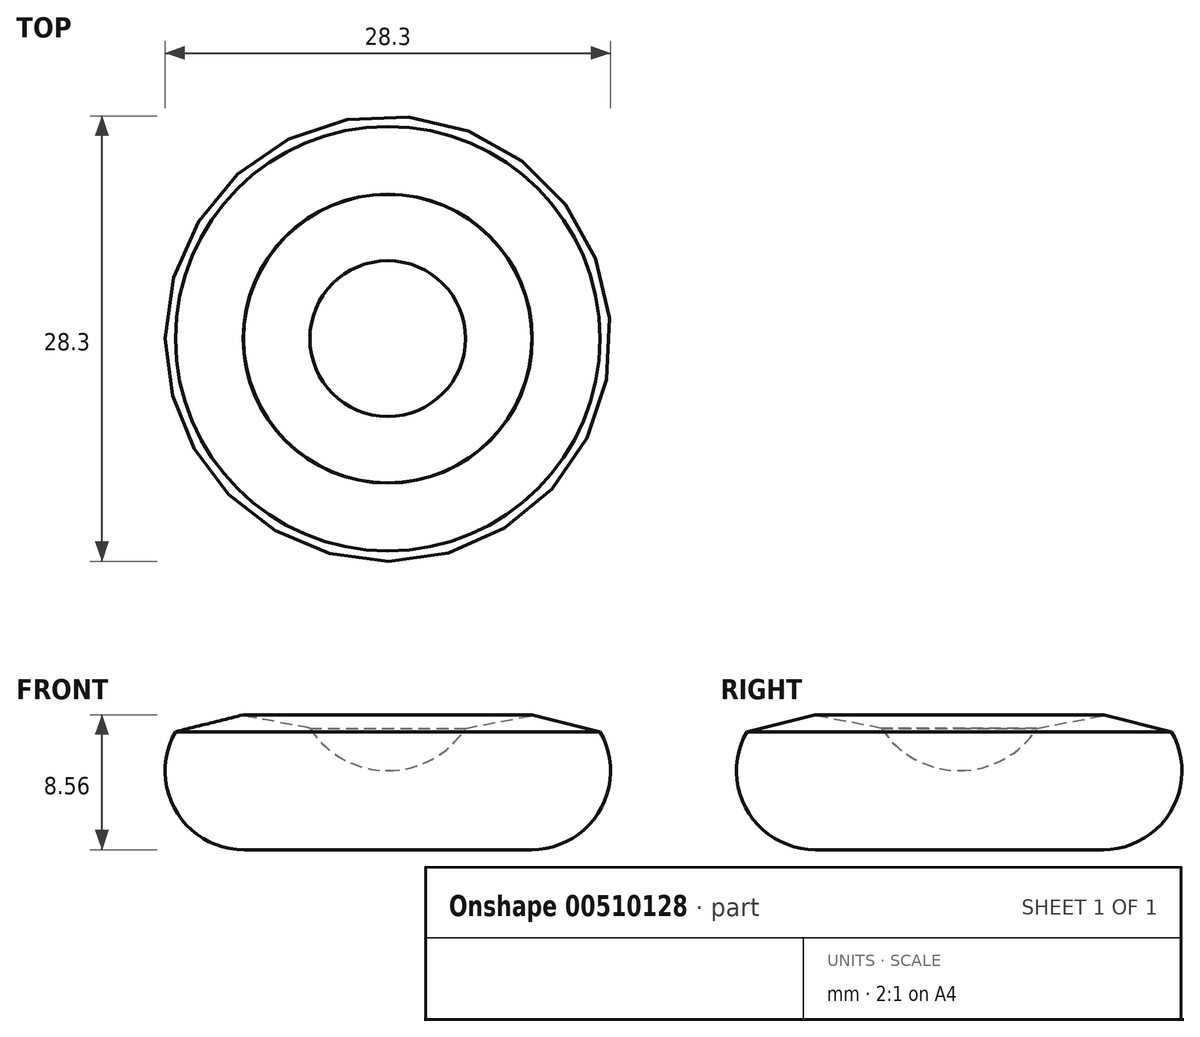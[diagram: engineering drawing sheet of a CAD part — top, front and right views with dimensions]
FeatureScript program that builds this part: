
annotation { "Feature Type Name" : "Feature", "Feature Type Description" : "" }
export const myFeature = defineFeature(function(context is Context, id is Id, definition is map)
    precondition{}
    {
        {
            var Q0;
            Q0=qCreatedBy(makeId("Front.planeOp"),FACE);
            var sketch = newSketch(context, id + "F0", { "sketchPlane" : qUnion([Q0])});
            skPoint(sketch, "E0.center.orphan", {"position": v(-21.03, 0) * mm});
            skPoint(sketch, "E1.center.orphan", {"position": v(-13.36, 0) * mm});
            skPoint(sketch, "E2.center.orphan", {"position": v(0, 5) * mm});
            skPoint(sketch, "E3.start.orphan", {"position": v(0, 1.96) * mm});
            skPoint(sketch, "E4.start.orphan", {"position": v(0, -5.22) * mm});
            skArc(sketch, "E5", {"start": v(-4.95, 7.7) * mm, "mid": v(-2.82, 5.72) * mm, "end": v(0, 5) * mm});
            skArc(sketch, "E6", {"start": v(-13.48, 7.47) * mm, "mid": v(-13.47, 2.47) * mm, "end": v(-9.14, -0.02) * mm});
            skLineSegment(sketch, "E7", {"start": v(0, 0) * mm, "end": v(-9.14, -0.02) * mm});
            skLineSegment(sketch, "E8", {"start": v(0, 0) * mm, "end": v(0, 5) * mm});
            skLineSegment(sketch, "E9.0", {"start": v(-4.95, 7.7) * mm, "end": v(-9.16, 8.5) * mm});
            skLineSegment(sketch, "E9.1", {"start": v(-9.16, 8.5) * mm, "end": v(-9.18, 8.54) * mm});
            skLineSegment(sketch, "E9.2", {"start": v(-9.18, 8.54) * mm, "end": v(-13.48, 7.47) * mm});
            skPoint(sketch, "E9.0.midPoint", {"position": v(-4.95, 7.7) * mm});
            skPoint(sketch, "E10.orphan", {"position": v(-22.33, 2.06) * mm});
            skPoint(sketch, "E11.orphan", {"position": v(-0.73, 6.9) * mm});
            skPoint(sketch, "E12.orphan", {"position": v(-31.57, 2.99) * mm});
            skSolve(sketch);
        }
        {
            var Q0;
            Q0=makeQuery(id+"F0.imprint","IMPRINT",FACE,{"disambiguationData":[TD([[makeQuery(id+"F0.imprint","IMPRINT",EDGE,{"derivedFrom":sQuery(id+"F0.wireOp",EDGE,"E5")}),-1.0]])]});
            var Q1;
            Q1=sQuery(id+"F0.wireOp",EDGE,"E8");
            revolve(context, id + "F1", {"entities" : qUnion([Q0]), "axis" : qUnion([Q1]), "revolveType" : RevolveType.FULL});
        }
    });
